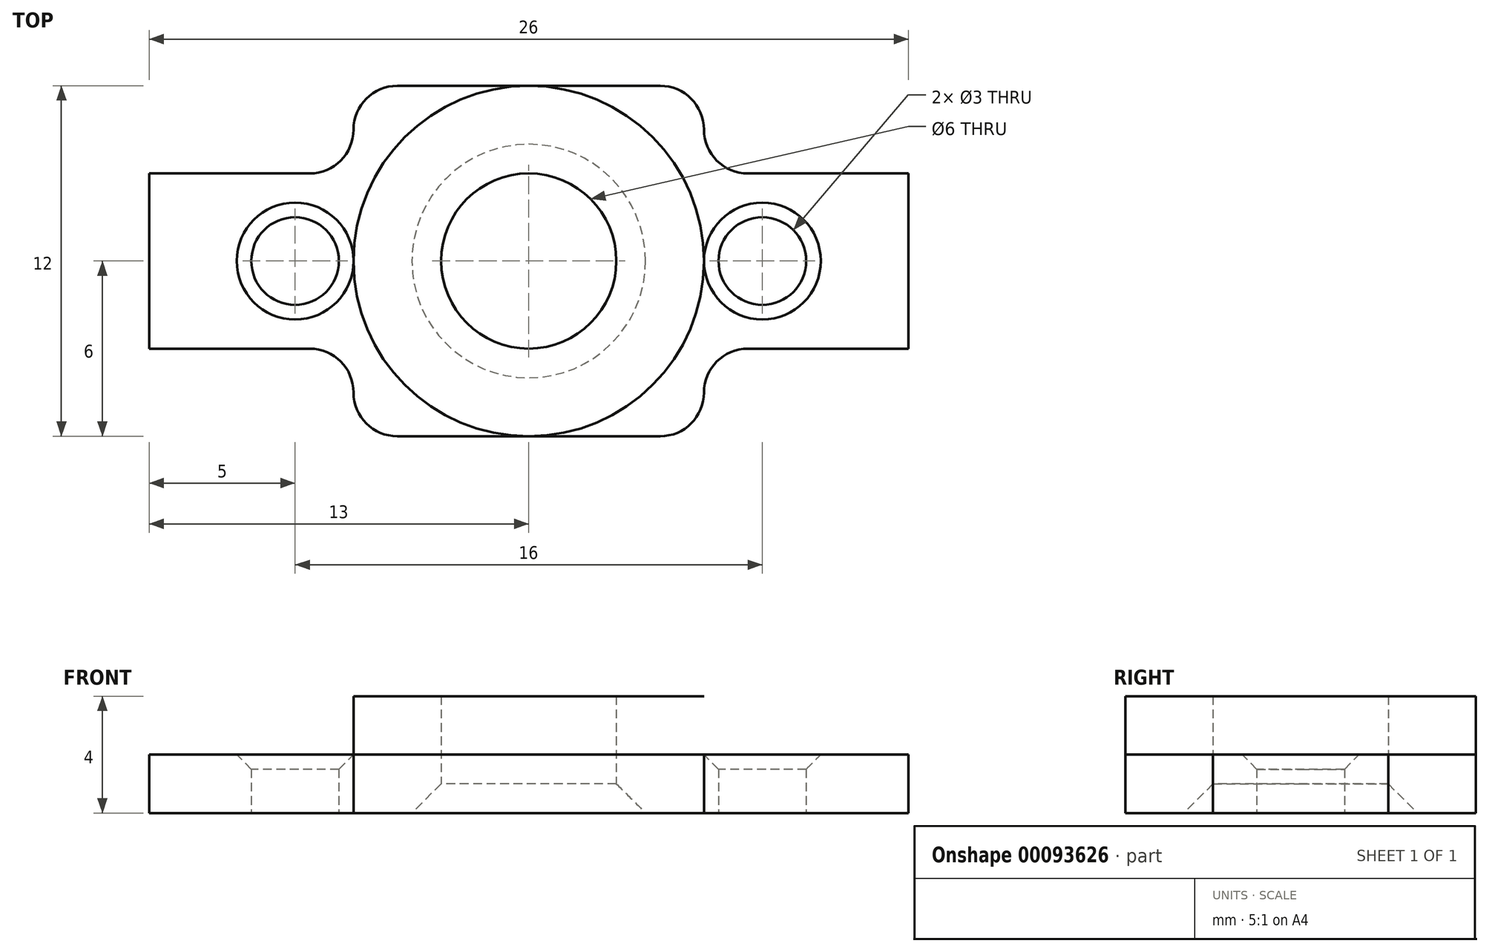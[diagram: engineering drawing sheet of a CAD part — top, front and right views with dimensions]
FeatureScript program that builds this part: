
annotation { "Feature Type Name" : "Feature", "Feature Type Description" : "" }
export const myFeature = defineFeature(function(context is Context, id is Id, definition is map)
    precondition{}
    {
        {
            var Q0;
            Q0=qCreatedBy(makeId("Top.planeOp"),FACE);
            var sketch = newSketch(context, id + "F0", { "sketchPlane" : qUnion([Q0])});
            skLineSegment(sketch, "E0.bottom", {"start": v(-13, 3) * mm, "end": v(13, 3) * mm, "construction": true});
            skLineSegment(sketch, "E0.top", {"start": v(-13, -3) * mm, "end": v(13, -3) * mm, "construction": true});
            skLineSegment(sketch, "E0.left", {"start": v(-13, 3) * mm, "end": v(-13, -3) * mm});
            skLineSegment(sketch, "E0.right", {"start": v(13, 3) * mm, "end": v(13, -3) * mm});
            skPoint(sketch, "E0.middle", {"position": v(0, 0) * mm});
            skLineSegment(sketch, "E1", {"start": v(-13, 3) * mm, "end": v(-6, 3) * mm});
            skLineSegment(sketch, "E2", {"start": v(-6, 3) * mm, "end": v(-6, 6) * mm});
            skLineSegment(sketch, "E3", {"start": v(-6, 6) * mm, "end": v(6, 6) * mm});
            skLineSegment(sketch, "E4", {"start": v(6, 6) * mm, "end": v(6, 3) * mm});
            skLineSegment(sketch, "E5", {"start": v(6, 3) * mm, "end": v(13, 3) * mm});
            skLineSegment(sketch, "E6", {"start": v(-13, -3) * mm, "end": v(-6, -3) * mm});
            skLineSegment(sketch, "E7", {"start": v(-6, -3) * mm, "end": v(-6, -6) * mm});
            skLineSegment(sketch, "E8", {"start": v(-6, -6) * mm, "end": v(6, -6) * mm});
            skLineSegment(sketch, "E9", {"start": v(6, -6) * mm, "end": v(6, -3) * mm});
            skLineSegment(sketch, "E10", {"start": v(6, -3) * mm, "end": v(13, -3) * mm});
            skCircle(sketch, "E11", {"center": v(0, 0) * mm, "radius": 3 * mm});
            skLineSegment(sketch, "E12", {"start": v(0, 0) * mm, "end": v(-8, 0) * mm, "construction": true});
            skLineSegment(sketch, "E13", {"start": v(0, 0) * mm, "end": v(8, 0) * mm, "construction": true});
            skCircle(sketch, "E14", {"center": v(-8, 0) * mm, "radius": 1.5 * mm});
            skCircle(sketch, "E15", {"center": v(8, 0) * mm, "radius": 1.5 * mm});
            skSolve(sketch);
        }
        {
            var Q0;
            Q0 = qSketchRegion(id + "F0", true);
            extrude(context, id + "F1", {"entities" : qUnion([Q0]), "depth" : 2 * mm});
        }
        {
            var Q0;
            Q0=makeQuery(id+"F1.opExtrude","CAP_FACE",FACE,{"disambiguationData":[OSD([sQuery(id+"F0.wireOp",EDGE,"E0.left"),sQuery(id+"F0.wireOp",EDGE,"E0.right"),sQuery(id+"F0.wireOp",EDGE,"E1"),sQuery(id+"F0.wireOp",EDGE,"E2"),sQuery(id+"F0.wireOp",EDGE,"E3"),sQuery(id+"F0.wireOp",EDGE,"E4"),sQuery(id+"F0.wireOp",EDGE,"E5"),sQuery(id+"F0.wireOp",EDGE,"E6"),sQuery(id+"F0.wireOp",EDGE,"E7"),sQuery(id+"F0.wireOp",EDGE,"E8"),sQuery(id+"F0.wireOp",EDGE,"E9"),sQuery(id+"F0.wireOp",EDGE,"E10"),sQuery(id+"F0.wireOp",EDGE,"E11"),sQuery(id+"F0.wireOp",EDGE,"E14"),sQuery(id+"F0.wireOp",EDGE,"E15")])],"isStart":false});
            var sketch = newSketch(context, id + "F2", { "sketchPlane" : qUnion([Q0])});
            skCircle(sketch, "E16", {"center": v(0, 0) * mm, "radius": 3 * mm});
            skCircle(sketch, "E17", {"center": v(0, 0) * mm, "radius": 6 * mm});
            skSolve(sketch);
        }
        {
            var Q0;
            Q0 = qSketchRegion(id + "F2", true);
            extrude(context, id + "F3", {"entities" : qUnion([Q0]), "operationType" : NewBodyOperationType.ADD, "depth" : 2 * mm});
        }
        {
            var Q0;
            Q0=makeQuery(id+"F1.opExtrude","SWEPT_EDGE",EDGE,{"disambiguationData":[OSD([sQuery(id+"F0.wireOp",EDGE,"E7"),sQuery(id+"F0.wireOp",EDGE,"E8")])]});
            var Q1;
            Q1=makeQuery(id+"F1.opExtrude","SWEPT_EDGE",EDGE,{"disambiguationData":[OSD([sQuery(id+"F0.wireOp",EDGE,"E8"),sQuery(id+"F0.wireOp",EDGE,"E9")])]});
            var Q2;
            Q2=makeQuery(id+"F1.opExtrude","SWEPT_EDGE",EDGE,{"disambiguationData":[OSD([sQuery(id+"F0.wireOp",EDGE,"E3"),sQuery(id+"F0.wireOp",EDGE,"E4")])]});
            var Q3;
            Q3=makeQuery(id+"F1.opExtrude","SWEPT_EDGE",EDGE,{"disambiguationData":[OSD([sQuery(id+"F0.wireOp",EDGE,"E2"),sQuery(id+"F0.wireOp",EDGE,"E3")])]});
            var Q4;
            Q4=makeQuery(id+"F1.opExtrude","SWEPT_EDGE",EDGE,{"disambiguationData":[OSD([sQuery(id+"F0.wireOp",EDGE,"E1"),sQuery(id+"F0.wireOp",EDGE,"E2")])]});
            var Q5;
            Q5=makeQuery(id+"F1.opExtrude","SWEPT_EDGE",EDGE,{"disambiguationData":[OSD([sQuery(id+"F0.wireOp",EDGE,"E6"),sQuery(id+"F0.wireOp",EDGE,"E7")])]});
            var Q6;
            Q6=makeQuery(id+"F1.opExtrude","SWEPT_EDGE",EDGE,{"disambiguationData":[OSD([sQuery(id+"F0.wireOp",EDGE,"E4"),sQuery(id+"F0.wireOp",EDGE,"E5")])]});
            var Q7;
            Q7=makeQuery(id+"F1.opExtrude","SWEPT_EDGE",EDGE,{"disambiguationData":[OSD([sQuery(id+"F0.wireOp",EDGE,"E9"),sQuery(id+"F0.wireOp",EDGE,"E10")])]});
            fillet(context, id + "F4", {"entities" : qUnion([Q0, Q1, Q2, Q3, Q4, Q5, Q6, Q7]), "radius" : 1.5 * mm, "tangentPropagation" : true, "allowEdgeOverflow" : false});
        }
        {
            var Q0;
            Q0=makeQuery(id+"F1.opExtrude","CAP_EDGE",EDGE,{"disambiguationData":[OSD([sQuery(id+"F0.wireOp",EDGE,"E11")])],"isStart":true});
            chamfer(context, id + "F5", {"entities" : qUnion([Q0]), "width" : 1 * mm, "tangentPropagation" : true});
        }
        {
            var Q0;
            Q0=makeQuery(id+"F1.opExtrude","CAP_EDGE",EDGE,{"disambiguationData":[OSD([sQuery(id+"F0.wireOp",EDGE,"E14")])],"isStart":false});
            var Q1;
            Q1=makeQuery(id+"F1.opExtrude","CAP_EDGE",EDGE,{"disambiguationData":[OSD([sQuery(id+"F0.wireOp",EDGE,"E15")])],"isStart":false});
            chamfer(context, id + "F6", {"entities" : qUnion([Q0, Q1]), "width" : 0.5 * mm, "tangentPropagation" : true});
        }
    });
